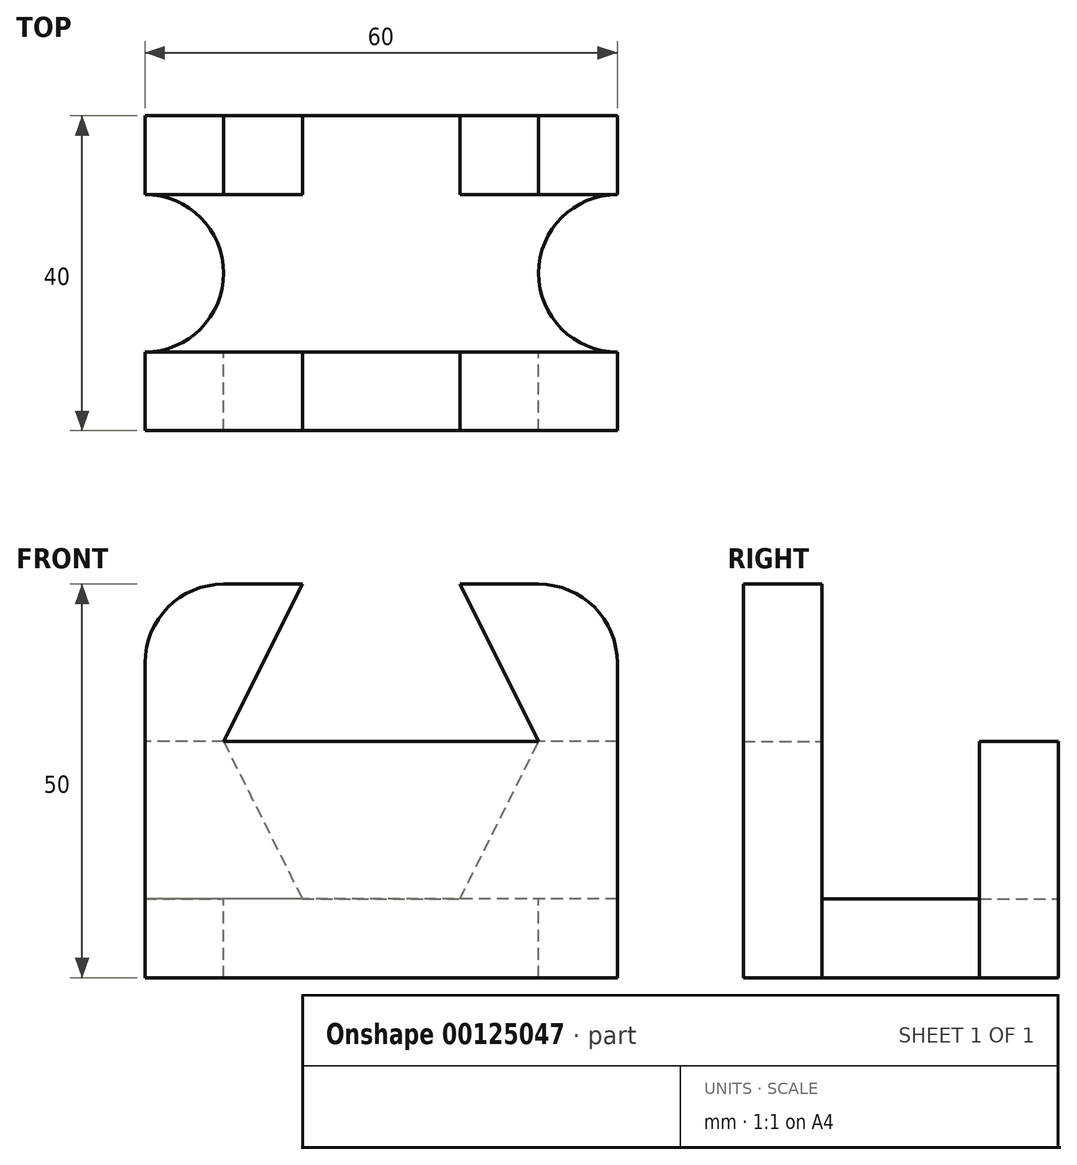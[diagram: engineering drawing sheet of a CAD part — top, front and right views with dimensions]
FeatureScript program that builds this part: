
annotation { "Feature Type Name" : "Feature", "Feature Type Description" : "" }
export const myFeature = defineFeature(function(context is Context, id is Id, definition is map)
    precondition{}
    {
        {
            var Q0;
            Q0=qCreatedBy(makeId("Right.planeOp"),FACE);
            var sketch = newSketch(context, id + "F0", { "sketchPlane" : qUnion([Q0])});
            skLineSegment(sketch, "E0", {"start": v(20, 0) * mm, "end": v(-20, 0) * mm});
            skLineSegment(sketch, "E1", {"start": v(-20, 0) * mm, "end": v(-20, 50) * mm});
            skLineSegment(sketch, "E2", {"start": v(-20, 50) * mm, "end": v(-10, 50) * mm});
            skLineSegment(sketch, "E3", {"start": v(-10, 50) * mm, "end": v(-10, 10) * mm});
            skLineSegment(sketch, "E4", {"start": v(-10, 10) * mm, "end": v(10, 10) * mm});
            skLineSegment(sketch, "E5", {"start": v(10, 10) * mm, "end": v(10, 30) * mm});
            skLineSegment(sketch, "E6", {"start": v(10, 30) * mm, "end": v(20, 30) * mm});
            skLineSegment(sketch, "E7", {"start": v(20, 30) * mm, "end": v(20, 0) * mm});
            skSolve(sketch);
        }
        {
            var Q0;
            Q0=makeQuery(id+"F0.imprint","IMPRINT",FACE,{"disambiguationData":[TD([[makeQuery(id+"F0.imprint","IMPRINT",EDGE,{"derivedFrom":sQuery(id+"F0.wireOp",EDGE,"E0")}),-1.0]])]});
            extrude(context, id + "F1", {"entities" : qUnion([Q0]), "endBound" : BoundingType.SYMMETRIC, "depth" : 60 * mm});
        }
        {
            var Q0;
            Q0=makeQuery(id+"F1.opExtrude","SWEPT_FACE",FACE,{"disambiguationData":[OSD([sQuery(id+"F0.wireOp",EDGE,"E7")])]});
            var sketch = newSketch(context, id + "F2", { "sketchPlane" : qUnion([Q0])});
            skLineSegment(sketch, "E8", {"start": v(-20, 30) * mm, "end": v(20, 30) * mm});
            skLineSegment(sketch, "E9", {"start": v(20, 30) * mm, "end": v(10, 10) * mm});
            skLineSegment(sketch, "E10", {"start": v(10, 10) * mm, "end": v(-10, 10) * mm});
            skLineSegment(sketch, "E11", {"start": v(-10, 10) * mm, "end": v(-20, 30) * mm});
            skSolve(sketch);
        }
        {
            var Q0;
            Q0=makeQuery(id+"F2.imprint","IMPRINT",FACE,{"disambiguationData":[TD([[makeQuery(id+"F2.imprint","IMPRINT",EDGE,{"derivedFrom":sQuery(id+"F2.wireOp",EDGE,"E8")}),-1.0]])]});
            extrude(context, id + "F3", {"entities" : qUnion([Q0]), "operationType" : NewBodyOperationType.REMOVE, "endBound" : BoundingType.UP_TO_NEXT, "oppositeDirection" : true, "depth" : 25 * mm});
        }
        {
            var Q0;
            Q0=makeQuery(id+"F1.opExtrude","SWEPT_FACE",FACE,{"disambiguationData":[OSD([sQuery(id+"F0.wireOp",EDGE,"E3")])]});
            var sketch = newSketch(context, id + "F4", { "sketchPlane" : qUnion([Q0])});
            skLineSegment(sketch, "E12", {"start": v(-10, 50) * mm, "end": v(-20, 30) * mm});
            skLineSegment(sketch, "E13", {"start": v(-20, 30) * mm, "end": v(20, 30) * mm});
            skLineSegment(sketch, "E14", {"start": v(20, 30) * mm, "end": v(10, 50) * mm});
            skLineSegment(sketch, "E15", {"start": v(10, 50) * mm, "end": v(-10, 50) * mm});
            skSolve(sketch);
        }
        {
            var Q0;
            Q0=makeQuery(id+"F4.imprint","IMPRINT",FACE,{"disambiguationData":[TD([[makeQuery(id+"F4.imprint","IMPRINT",EDGE,{"derivedFrom":sQuery(id+"F4.wireOp",EDGE,"E12")}),1.0]])]});
            extrude(context, id + "F5", {"entities" : qUnion([Q0]), "operationType" : NewBodyOperationType.REMOVE, "endBound" : BoundingType.UP_TO_NEXT, "oppositeDirection" : true, "depth" : 25 * mm});
        }
        {
            var Q0;
            Q0=makeQuery(id+"F3.boolean.opBoolean","MERGE",FACE,{"derivedFrom":[makeQuery(id+"F1.opExtrude","SWEPT_FACE",FACE,{"disambiguationData":[OSD([sQuery(id+"F0.wireOp",EDGE,"E4")])]}),makeQuery(id+"F3.opExtrude","SWEPT_FACE",FACE,{"disambiguationData":[OSD([sQuery(id+"F2.wireOp",EDGE,"E10")])]})]});
            var sketch = newSketch(context, id + "F6", { "sketchPlane" : qUnion([Q0])});
            skCircle(sketch, "E16", {"center": v(-30, 0) * mm, "radius": 10 * mm});
            skCircle(sketch, "E17", {"center": v(30, 0) * mm, "radius": 10 * mm});
            skSolve(sketch);
        }
        {
            var Q0;
            {var subQ1=sQuery(id+"F0.wireOp",EDGE,"E4");var subQ2=makeQuery(id+"F1.opExtrude","CAP_EDGE",EDGE,{"disambiguationData":[OSD([subQ1])],"isStart":true});Q0=makeQuery(id+"F6.imprint","IMPRINT",FACE,{"disambiguationData":[TD([[makeQuery(id+"F6.imprint","IMPRINT",EDGE,{"derivedFrom":subQ2}),-1.0]])]});}
            var Q1;
            {var subQ1=sQuery(id+"F0.wireOp",EDGE,"E4");var subQ2=makeQuery(id+"F1.opExtrude","CAP_EDGE",EDGE,{"disambiguationData":[OSD([subQ1])],"isStart":false});Q1=makeQuery(id+"F6.imprint","IMPRINT",FACE,{"disambiguationData":[TD([[makeQuery(id+"F6.imprint","IMPRINT",EDGE,{"derivedFrom":subQ2}),1.0]])]});}
            extrude(context, id + "F7", {"entities" : qUnion([Q0, Q1]), "operationType" : NewBodyOperationType.REMOVE, "endBound" : BoundingType.UP_TO_NEXT, "oppositeDirection" : true, "depth" : 25 * mm});
        }
        {
            var Q0;
            Q0=makeQuery(id+"F1.opExtrude","CAP_EDGE",EDGE,{"disambiguationData":[OSD([sQuery(id+"F0.wireOp",EDGE,"E2")])],"isStart":false});
            var Q1;
            Q1=makeQuery(id+"F1.opExtrude","CAP_EDGE",EDGE,{"disambiguationData":[OSD([sQuery(id+"F0.wireOp",EDGE,"E2")])],"isStart":true});
            fillet(context, id + "F8", {"entities" : qUnion([Q0, Q1]), "radius" : 10 * mm, "tangentPropagation" : true, "allowEdgeOverflow" : false});
        }
    });
